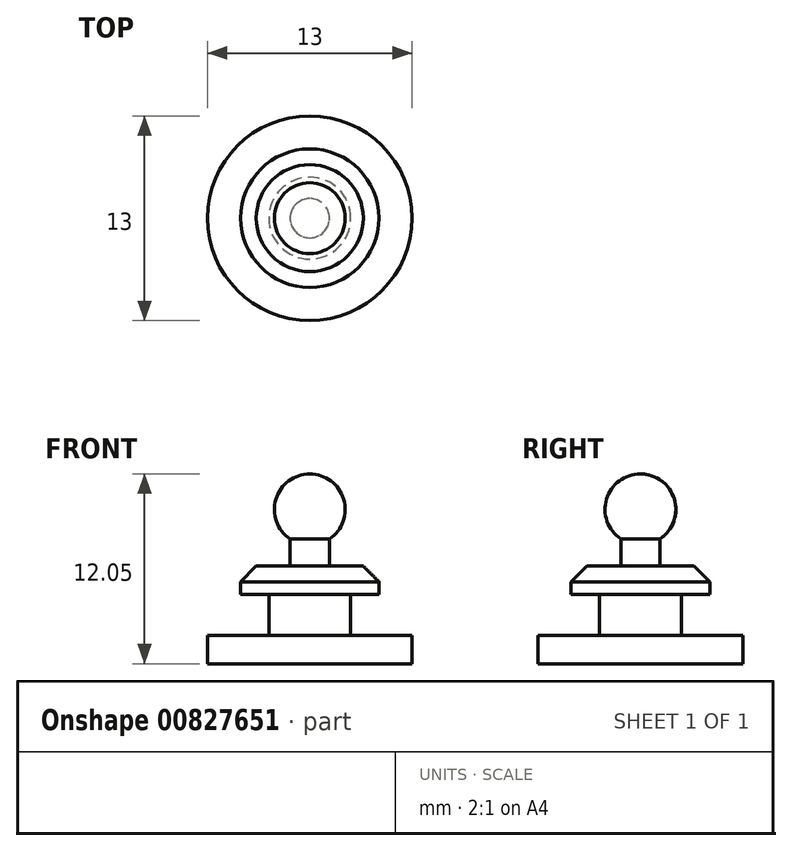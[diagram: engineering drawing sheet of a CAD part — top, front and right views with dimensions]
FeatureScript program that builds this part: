
annotation { "Feature Type Name" : "Feature", "Feature Type Description" : "" }
export const myFeature = defineFeature(function(context is Context, id is Id, definition is map)
    precondition{}
    {
        {
            var Q0;
            Q0=qCreatedBy(makeId("Top.planeOp"),FACE);
            var sketch = newSketch(context, id + "F0", { "sketchPlane" : qUnion([Q0])});
            skCircle(sketch, "E0", {"center": v(0, 0) * mm, "radius": 6.5 * mm});
            skSolve(sketch);
        }
        {
            var Q0;
            Q0 = qSketchRegion(id + "F0", true);
            extrude(context, id + "F1", {"entities" : qUnion([Q0]), "depth" : 1.8 * mm, "offsetDistance" : 25 * mm});
        }
        {
            var Q0;
            Q0=makeQuery(id+"F1.opExtrude","CAP_FACE",FACE,{"disambiguationData":[OSD([sQuery(id+"F0.wireOp",EDGE,"E0")])],"isStart":false});
            var sketch = newSketch(context, id + "F2", { "sketchPlane" : qUnion([Q0])});
            skCircle(sketch, "E1", {"center": v(0, 0) * mm, "radius": 2.6 * mm});
            skSolve(sketch);
        }
        {
            var Q0;
            Q0=makeQuery(id+"F1.opExtrude","CAP_FACE",FACE,{"disambiguationData":[OSD([sQuery(id+"F0.wireOp",EDGE,"E0")])],"isStart":false});
            cPlane(context, id + "F3", {"entities" : qUnion([Q0]), "cplaneType" : CPlaneType.OFFSET, "offset" : 4.4 * mm, "width" : 150 * mm, "height" : 150 * mm});
        }
        {
            var Q0;
            Q0 = qSketchRegion(id + "F2", true);
            extrude(context, id + "F4", {"entities" : qUnion([Q0]), "operationType" : NewBodyOperationType.ADD, "depth" : 2.6 * mm, "offsetDistance" : 25 * mm});
        }
        {
            var Q0;
            Q0=makeQuery(id+"F4.opExtrude","CAP_FACE",FACE,{"disambiguationData":[OSD([sQuery(id+"F2.wireOp",EDGE,"E1")])],"isStart":false});
            var sketch = newSketch(context, id + "F5", { "sketchPlane" : qUnion([Q0])});
            skCircle(sketch, "E2", {"center": v(0, 0) * mm, "radius": 4.4 * mm});
            skSolve(sketch);
        }
        {
            var Q0;
            Q0 = qSketchRegion(id + "F5", true);
            var Q1;
            Q1=qCreatedBy(id+"F3.planeOp",FACE);
            extrude(context, id + "F6", {"entities" : qUnion([Q0]), "operationType" : NewBodyOperationType.ADD, "endBound" : BoundingType.UP_TO_SURFACE, "depth" : 25 * mm, "endBoundEntityFace" : qUnion([Q1]), "offsetDistance" : 25 * mm});
        }
        {
            var Q0;
            Q0=makeQuery(id+"F6.opExtrude","CAP_EDGE",EDGE,{"disambiguationData":[OSD([sQuery(id+"F5.wireOp",EDGE,"E2")])],"isStart":false});
            chamfer(context, id + "F7", {"entities" : qUnion([Q0]), "width" : 1 * mm, "tangentPropagation" : true});
        }
        {
            var Q0;
            Q0=makeQuery(id+"F6.opExtrude","CAP_FACE",FACE,{"disambiguationData":[OSD([sQuery(id+"F5.wireOp",EDGE,"E2")])],"isStart":false});
            var sketch = newSketch(context, id + "F8", { "sketchPlane" : qUnion([Q0])});
            skCircle(sketch, "E3", {"center": v(0, 0) * mm, "radius": 1.25 * mm});
            skSolve(sketch);
        }
        {
            var Q0;
            Q0 = qSketchRegion(id + "F8", true);
            extrude(context, id + "F9", {"entities" : qUnion([Q0]), "operationType" : NewBodyOperationType.ADD, "depth" : 1.8 * mm, "offsetDistance" : 25 * mm});
        }
        {
            var Q0;
            Q0=qCreatedBy(makeId("Right.planeOp"),FACE);
            var sketch = newSketch(context, id + "F10", { "sketchPlane" : qUnion([Q0])});
            skLineSegment(sketch, "E4", {"start": v(0, 7.55) * mm, "end": v(0, 12.05) * mm});
            skArc(sketch, "E5", {"start": v(0, 7.55) * mm, "mid": v(2.25, 9.8) * mm, "end": v(0, 12.05) * mm});
            skPoint(sketch, "E6.orphan", {"position": v(0, -3.66) * mm});
            skSolve(sketch);
        }
        {
            var Q0;
            Q0 = qSketchRegion(id + "F10", true);
            var Q1;
            Q1=sQuery(id+"F10.wireOp",EDGE,"E4");
            revolve(context, id + "F11", {"operationType" : NewBodyOperationType.ADD, "surfaceOperationType" : NewSurfaceOperationType.NEW, "entities" : qUnion([Q0]), "axis" : qUnion([Q1]), "revolveType" : RevolveType.FULL});
        }
    });
